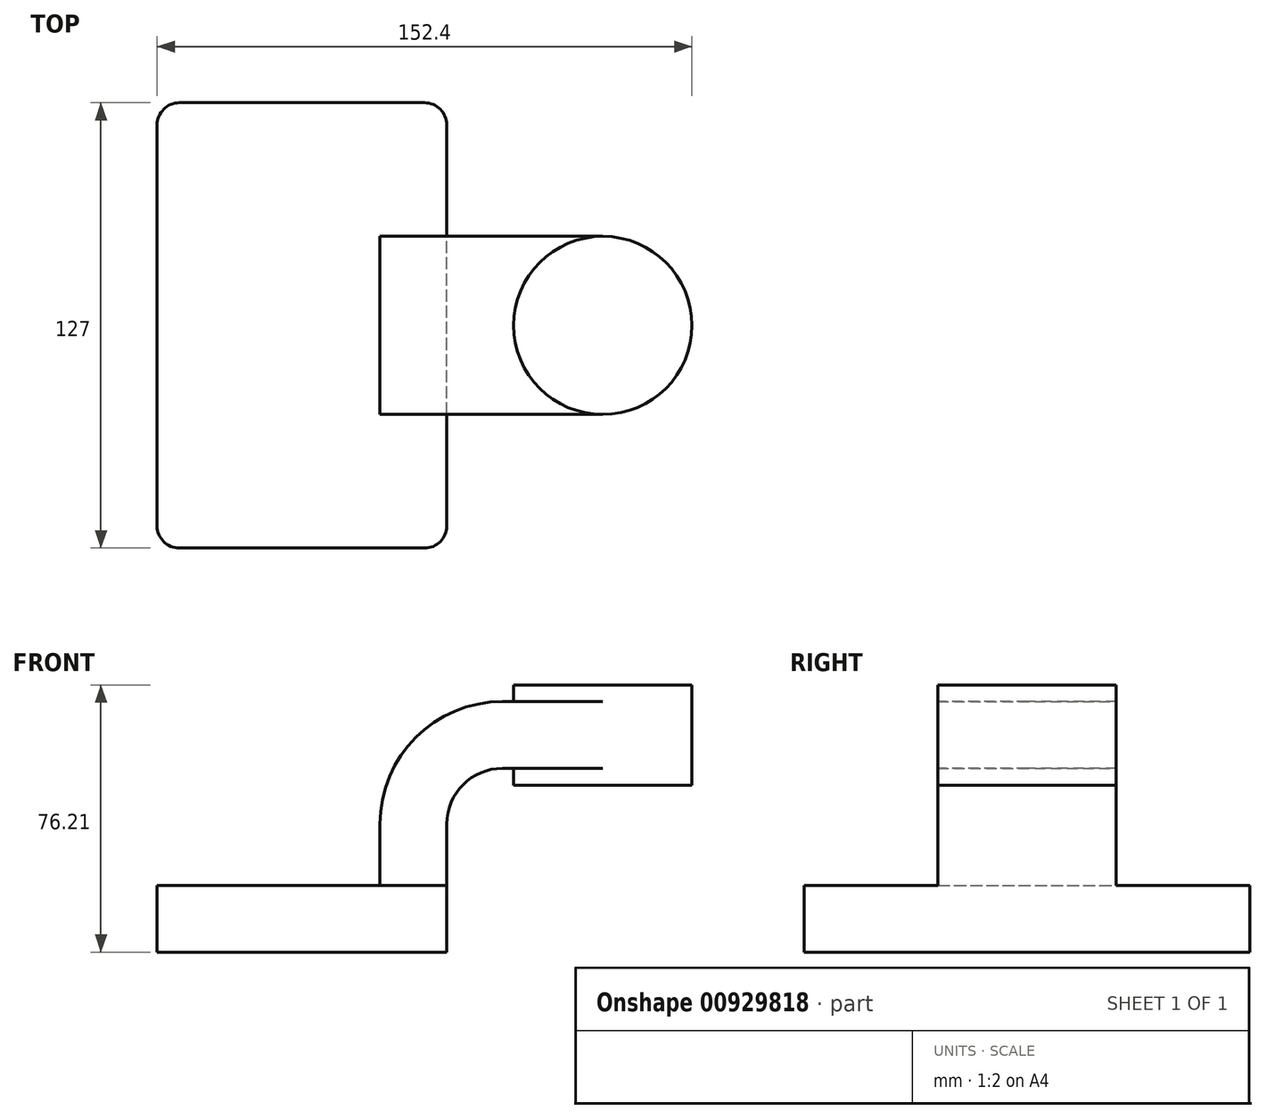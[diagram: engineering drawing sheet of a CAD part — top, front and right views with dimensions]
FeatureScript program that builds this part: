
annotation { "Feature Type Name" : "Feature", "Feature Type Description" : "" }
export const myFeature = defineFeature(function(context is Context, id is Id, definition is map)
    precondition{}
    {
        {
            var Q0;
            Q0=qCreatedBy(makeId("Front.planeOp"),FACE);
            var sketch = newSketch(context, id + "F0", { "sketchPlane" : qUnion([Q0])});
            skLineSegment(sketch, "E0.bottom", {"start": v(-41.28, 9.53) * mm, "end": v(41.28, 9.53) * mm});
            skLineSegment(sketch, "E0.top", {"start": v(-41.28, -9.53) * mm, "end": v(41.28, -9.53) * mm});
            skLineSegment(sketch, "E0.left", {"start": v(-41.28, 9.53) * mm, "end": v(-41.28, -9.53) * mm});
            skLineSegment(sketch, "E0.right", {"start": v(41.28, 9.53) * mm, "end": v(41.28, -9.53) * mm});
            skPoint(sketch, "E0.middle", {"position": v(0, 0) * mm});
            skLineSegment(sketch, "E1", {"start": v(41.28, 9.52) * mm, "end": v(41.28, 27) * mm});
            skLineSegment(sketch, "E2.bottom", {"start": v(60.32, 38.1) * mm, "end": v(111.12, 38.1) * mm});
            skLineSegment(sketch, "E2.top", {"start": v(60.32, 66.67) * mm, "end": v(111.12, 66.67) * mm});
            skLineSegment(sketch, "E2.left", {"start": v(60.32, 38.1) * mm, "end": v(60.32, 66.67) * mm});
            skLineSegment(sketch, "E2.right", {"start": v(111.13, 38.1) * mm, "end": v(111.13, 66.67) * mm});
            skPoint(sketch, "E2.middle", {"position": v(85.72, 52.39) * mm});
            skLineSegment(sketch, "E3", {"start": v(57.15, 42.88) * mm, "end": v(85.72, 42.88) * mm});
            skArc(sketch, "E4", {"start": v(41.27, 27) * mm, "mid": v(45.92, 38.23) * mm, "end": v(57.15, 42.88) * mm});
            skLineSegment(sketch, "E5.0", {"start": v(57.15, 61.93) * mm, "end": v(85.72, 61.93) * mm});
            skArc(sketch, "E5.1", {"start": v(22.22, 27) * mm, "mid": v(32.45, 51.7) * mm, "end": v(57.15, 61.93) * mm});
            skLineSegment(sketch, "E5.2", {"start": v(22.22, 9.52) * mm, "end": v(22.22, 27) * mm});
            skLineSegment(sketch, "E6", {"start": v(85.72, 38.1) * mm, "end": v(85.72, 66.67) * mm});
            skFitSpline(sketch, "E7", {"points": [v(-41.28, 9.53) * mm, v(57.15, 61.93) * mm], "startDerivative": vector(0, 50.34) * mm, "endDerivative": vector(138.92, -2.8) * mm});
            skSolve(sketch);
        }
        {
            var Q0;
            Q0=makeQuery(id+"F0.imprint","IMPRINT",FACE,{"disambiguationData":[TD([[makeQuery(id+"F0.imprint","IMPRINT",EDGE,{"derivedFrom":sQuery(id+"F0.wireOp",EDGE,"E0.top")}),1.0]])]});
            extrude(context, id + "F1", {"entities" : qUnion([Q0]), "endBound" : BoundingType.SYMMETRIC, "depth" : 127 * mm, "offsetDistance" : 25.4 * mm});
        }
        {
            var Q0;
            {var subQ4=sQuery(id+"F0.wireOp",EDGE,"E1");Q0=makeQuery(id+"F0.imprint","IMPRINT",FACE,{"disambiguationData":[TD([[makeQuery(id+"F0.imprint","IMPRINT",EDGE,{"derivedFrom":subQ4}),1.0]])]});}
            var Q1;
            {var subQ0=sQuery(id+"F0.wireOp",EDGE,"E3");var subQ1=sQuery(id+"F0.wireOp",EDGE,"E2.left");var subQ2=makeQuery(id+"F0.imprint","INTERSECT",VERTEX,{"derivedFrom":[subQ1,subQ0]});Q1=makeQuery(id+"F0.imprint","IMPRINT",FACE,{"disambiguationData":[TD([[makeQuery(id+"F0.imprint","IMPRINT",EDGE,{"disambiguationData":[TD([[subQ2,-1.0]])],"derivedFrom":subQ1}),-1.0]])]});}
            extrude(context, id + "F2", {"entities" : qUnion([Q0, Q1]), "operationType" : NewBodyOperationType.ADD, "endBound" : BoundingType.SYMMETRIC, "depth" : 50.8 * mm, "offsetDistance" : 25.4 * mm});
        }
        {
            var Q0;
            Q0=makeQuery(id+"F0.imprint","IMPRINT",FACE,{"disambiguationData":[TD([[makeQuery(id+"F0.imprint","IMPRINT",EDGE,{"derivedFrom":sQuery(id+"F0.wireOp",EDGE,"E5.1")}),1.0]])]});
            extrude(context, id + "F3", {"entities" : qUnion([Q0]), "operationType" : NewBodyOperationType.ADD, "endBound" : BoundingType.SYMMETRIC, "depth" : 15.88 * mm, "offsetDistance" : 25.4 * mm});
        }
        {
            var Q0;
            {var subQ4=sQuery(id+"F0.wireOp",EDGE,"E2.right");Q0=makeQuery(id+"F0.imprint","IMPRINT",FACE,{"disambiguationData":[TD([[makeQuery(id+"F0.imprint","IMPRINT",EDGE,{"derivedFrom":subQ4}),1.0]])]});}
            var Q1;
            Q1=sQuery(id+"F0.wireOp",EDGE,"E6");
            revolve(context, id + "F4", {"operationType" : NewBodyOperationType.ADD, "surfaceOperationType" : NewSurfaceOperationType.NEW, "entities" : qUnion([Q0]), "axis" : qUnion([Q1]), "revolveType" : RevolveType.FULL});
        }
        {
            var Q0;
            Q0=makeQuery(id+"F1.opExtrude","CAP_EDGE",EDGE,{"disambiguationData":[OSD([sQuery(id+"F0.wireOp",EDGE,"E0.left")])],"isStart":false});
            var Q1;
            Q1=makeQuery(id+"F1.opExtrude","CAP_EDGE",EDGE,{"disambiguationData":[OSD([sQuery(id+"F0.wireOp",EDGE,"E0.right")])],"isStart":false});
            var Q2;
            Q2=makeQuery(id+"F1.opExtrude","CAP_EDGE",EDGE,{"disambiguationData":[OSD([sQuery(id+"F0.wireOp",EDGE,"E0.right")])],"isStart":true});
            var Q3;
            Q3=makeQuery(id+"F1.opExtrude","CAP_EDGE",EDGE,{"disambiguationData":[OSD([sQuery(id+"F0.wireOp",EDGE,"E0.left")])],"isStart":true});
            fillet(context, id + "F5", {"entities" : qUnion([Q0, Q1, Q2, Q3]), "radius" : 6.35 * mm, "tangentPropagation" : true, "allowEdgeOverflow" : false});
        }
    });
